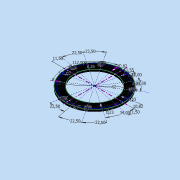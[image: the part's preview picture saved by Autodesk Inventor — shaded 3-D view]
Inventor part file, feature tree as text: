
AUTODESK INVENTOR PART (.ipt)
format: ipt  version: 2015 (Build 190159000, 159)  size: 3,002,880 bytes
history: native  units: mm
features: extrude x24, other x12, sketch x8
ambient origin geometry x8: Origin, YZ Plane, XZ Plane, XY Plane, X Axis, Y Axis, Z Axis, Center Point
bodies: Volumenkörper1 (feature_tree)
feature tree (44):
  extrude  "Extrusion1"  Depth=31.7mm
  sketch  "Skizze4"  dims[d2=1.65mm d3=0.0mm d11=42.0mm]
  extrude  "Extrusion2"  Depth=42.0mm
  extrude  "Extrusion3"  Depth=2.0mm
  extrude  "Extrusion4"  Depth=0.01mm TaperAngle=0.0deg
  extrude  "Extrusion5"  Depth=0.01mm TaperAngle=0.0deg
  extrude  "Extrusion6"  Depth=0.01mm TaperAngle=0.0deg
  extrude  "Extrusion7"  Depth=0.01mm TaperAngle=0.0deg
  other  "Prägen1"
  other  "Prägen2"
  extrude  "Extrusion8"  Depth=0.01mm
  extrude  "Extrusion9"  Depth=0.01mm
  extrude  "Extrusion10"  Depth=0.01mm TaperAngle=0.0deg
  other  "Prägen3"
  extrude  "Extrusion11"  Depth=0.01mm TaperAngle=112.5deg
  extrude  "Extrusion12"  Depth=0.01mm TaperAngle=0.0deg
  extrude  "Extrusion13"  Depth=0.01mm TaperAngle=0.0deg
  other  "Prägen4"
  extrude  "Extrusion14"  Depth=0.01mm
  extrude  "Extrusion15"  Depth=0.01mm
  extrude  "Extrusion16"  Depth=0.01mm TaperAngle=0.0deg
  other  "Prägen5"
  other  "Prägen6"
  extrude  "Extrusion17"  Depth=0.01mm
  extrude  "Extrusion18"  Depth=0.01mm TaperAngle=0.0deg
  extrude  "Extrusion19"  Depth=0.01mm
  extrude  "Extrusion20"  Depth=0.01mm
  extrude  "Extrusion21"  Depth=0.01mm
  extrude  "Extrusion22"  Depth=0.01mm TaperAngle=0.0deg
  extrude  "Extrusion23"  Depth=0.01mm TaperAngle=0.0deg
  extrude  "Extrusion24"  Depth=0.01mm
  sketch  "Skizze10"  dims[d28=0.01mm d29=0.0mm d30=1.889218mm d31=2.015856mm d32=0.01mm d33=0.0mm d34=20.0mm d36=112.5deg d38=0.01mm d39=0.0mm d40=0.01mm d41=0.0mm d42=2.0mm d43=2.0mm d44=0.01mm d45=0.0mm d47=20.0mm d48=0.01mm d49=0.0mm d50=1.888446mm d51=1.23mm d52=2.0mm d53=0.01mm d54=0.0mm d55=0.01mm d56=0.0mm d57=2.0mm d58=0.01mm d59=0.0mm d60=0.01mm d61=0.0mm d62=5.934119mm d63=1.23mm d64=2.0mm d65=0.01mm d66=0.0mm d67=0.01mm d68=0.0mm d69=2.0mm d70=0.01mm d71=0.0mm d72=0.01mm d73=0.0mm d74=3.839724mm d75=0.95mm d76=0.01mm d77=0.0mm d78=4.014257mm d79=0.5mm d80=0.9mm d82=20.0mm d83=0.5mm d84=0.9mm d85=0.8mm d86=0.01mm d87=0.0mm d89=2.007129mm d92=20.0mm d94=315.0deg d96=0.01mm d97=0.0mm d98=22.5deg d100=20.0mm d102=20.0mm d103=0.5mm d104=0.9mm d105=0.5mm d106=0.9mm d107=0.8mm d108=0.01mm d109=0.0mm d110=22.5deg d112=20.0mm d114=20.0mm d115=0.95mm d116=0.01mm d117=0.0mm d118=22.5deg d120=20.0mm d122=20.0mm d123=0.5mm d124=0.9mm d125=0.5mm d126=0.9mm d127=0.8mm d128=0.01mm d129=0.0mm d130=2.007129mm d132=20.0mm d134=20.0mm d135=0.5mm d136=0.9mm d137=0.5mm d138=0.9mm d139=0.8mm d140=0.01mm d141=0.0mm d142=22.5deg d144=20.0mm d146=20.0mm d147=0.95mm d148=0.01mm d149=0.0mm d150=22.5deg d152=20.0mm d154=20.0mm d155=0.5mm d156=0.9mm d157=0.5mm d158=0.9mm d159=0.8mm d160=0.01mm d161=0.0mm d162=0.01mm d163=0.0mm d164=0.01mm d165=0.0mm d166=0.01mm d167=0.0mm d168=0.01mm d169=0.0mm d170=0.01mm d171=0.0mm d172=0.01mm d173=0.0mm]
  other  "Prägen7"
  other  "Prägen8"
  other  "Prägen9"
  other  "Prägen10"
  other  "Prägen11"
  other  "Prägen12"
  sketch  "Skizze1"  dims[d0=44.2mm d1=31.7mm]
  sketch  "Skizze5"  dims[d12=1.23mm d13=2.0mm]
  sketch  "Skizze6"  dims[d14=1.65mm d15=0.0mm d16=0.01mm d17=0.0mm]
  sketch  "Skizze7"  dims[d18=2.0mm d19=0.01mm d20=0.0mm]
  sketch  "Skizze8"  dims[d21=0.01mm d22=0.0mm d23=0.01mm d24=0.0mm]
  sketch  "Skizze9"  dims[d25=2.0mm d26=0.01mm d27=0.0mm]
